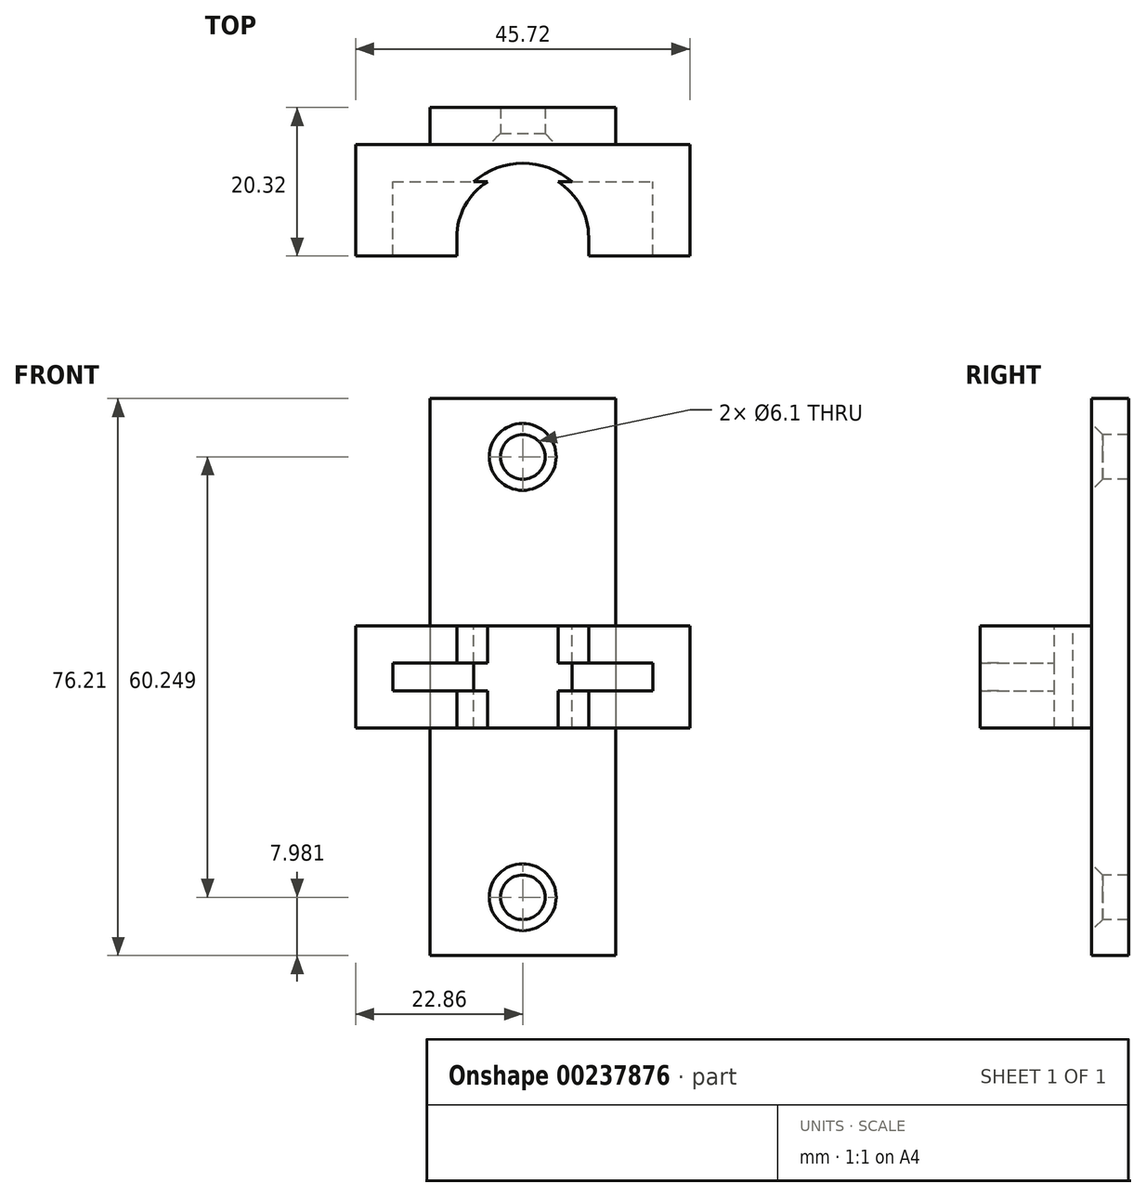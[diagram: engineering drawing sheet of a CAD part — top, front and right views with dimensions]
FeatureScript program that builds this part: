
annotation { "Feature Type Name" : "Feature", "Feature Type Description" : "" }
export const myFeature = defineFeature(function(context is Context, id is Id, definition is map)
    precondition{}
    {
        {
            var Q0;
            Q0=qCreatedBy(makeId("Top.planeOp"),FACE);
            var sketch = newSketch(context, id + "F0", { "sketchPlane" : qUnion([Q0])});
            skCircle(sketch, "E0", {"center": v(0, -0.94) * mm, "radius": 9.02 * mm});
            skCircle(sketch, "E1", {"center": v(0, -0.94) * mm, "radius": 10.16 * mm});
            skLineSegment(sketch, "E2.top", {"start": v(22.86, 11.76) * mm, "end": v(-22.86, 11.76) * mm});
            skLineSegment(sketch, "E2.left", {"start": v(22.86, -3.48) * mm, "end": v(22.86, 11.76) * mm});
            skLineSegment(sketch, "E2.right", {"start": v(-22.86, -3.48) * mm, "end": v(-22.86, 11.76) * mm});
            skPoint(sketch, "E3", {"position": v(0, -3.48) * mm});
            skLineSegment(sketch, "E4", {"start": v(-22.86, -3.48) * mm, "end": v(22.86, -3.48) * mm});
            skLineSegment(sketch, "E5", {"start": v(-10.16, -0.94) * mm, "end": v(-10.16, -3.48) * mm});
            skLineSegment(sketch, "E6", {"start": v(10.16, -0.94) * mm, "end": v(10.16, -3.48) * mm});
            skLineSegment(sketch, "E7.bottom", {"start": v(-17.78, -3.48) * mm, "end": v(17.78, -3.48) * mm});
            skLineSegment(sketch, "E7.top", {"start": v(-17.78, 6.68) * mm, "end": v(17.78, 6.68) * mm});
            skLineSegment(sketch, "E7.left", {"start": v(-17.78, -3.48) * mm, "end": v(-17.78, 6.68) * mm});
            skLineSegment(sketch, "E7.right", {"start": v(17.78, -3.48) * mm, "end": v(17.78, 6.68) * mm});
            skLineSegment(sketch, "E8", {"start": v(-9.02, -0.94) * mm, "end": v(-9.02, -3.48) * mm, "construction": true});
            skLineSegment(sketch, "E9", {"start": v(9.02, -0.94) * mm, "end": v(9.02, -3.48) * mm, "construction": true});
            skLineSegment(sketch, "E10.bottom", {"start": v(-9.02, -0.94) * mm, "end": v(9.02, -0.94) * mm});
            skLineSegment(sketch, "E10.top", {"start": v(-9.02, -3.48) * mm, "end": v(9.02, -3.48) * mm});
            skLineSegment(sketch, "E10.left", {"start": v(-9.02, -0.94) * mm, "end": v(-9.02, -3.48) * mm});
            skLineSegment(sketch, "E10.right", {"start": v(9.02, -0.94) * mm, "end": v(9.02, -3.48) * mm});
            skSolve(sketch);
        }
        {
            var Q0;
            {var subQ1=sQuery(id+"F0.wireOp",EDGE,"E5");Q0=makeQuery(id+"F0.imprint","IMPRINT",FACE,{"disambiguationData":[TD([[makeQuery(id+"F0.imprint","IMPRINT",EDGE,{"derivedFrom":subQ1}),-1.0]])]});}
            var Q1;
            {var subQ5=sQuery(id+"F0.wireOp",EDGE,"E6");Q1=makeQuery(id+"F0.imprint","IMPRINT",FACE,{"disambiguationData":[TD([[makeQuery(id+"F0.imprint","IMPRINT",EDGE,{"derivedFrom":subQ5}),1.0]])]});}
            var Q2;
            {var subQ0=sQuery(id+"F0.wireOp",EDGE,"E10.left");Q2=makeQuery(id+"F0.imprint","IMPRINT",FACE,{"disambiguationData":[TD([[makeQuery(id+"F0.imprint","IMPRINT",EDGE,{"derivedFrom":subQ0}),-1.0]])]});}
            var Q3;
            {var subQ4=sQuery(id+"F0.wireOp",EDGE,"E10.right");Q3=makeQuery(id+"F0.imprint","IMPRINT",FACE,{"disambiguationData":[TD([[makeQuery(id+"F0.imprint","IMPRINT",EDGE,{"derivedFrom":subQ4}),1.0]])]});}
            var Q4;
            {var subQ0=sQuery(id+"F0.wireOp",EDGE,"E7.top");var subQ1=sQuery(id+"F0.wireOp",EDGE,"E0");var subQ2=makeQuery(id+"F0.imprint","INTERSECT",VERTEX,{"disambiguationData":[OD(0.0)],"derivedFrom":[subQ1,subQ0]});Q4=makeQuery(id+"F0.imprint","IMPRINT",FACE,{"disambiguationData":[TD([[makeQuery(id+"F0.imprint","IMPRINT",EDGE,{"disambiguationData":[TD([[subQ2,-1.0]])],"derivedFrom":subQ1}),-1.0]])]});}
            var Q5;
            {var subQ0=sQuery(id+"F0.wireOp",EDGE,"E5");Q5=makeQuery(id+"F0.imprint","IMPRINT",FACE,{"disambiguationData":[TD([[makeQuery(id+"F0.imprint","IMPRINT",EDGE,{"derivedFrom":subQ0}),1.0]])]});}
            var Q6;
            {var subQ0=sQuery(id+"F0.wireOp",EDGE,"E6");Q6=makeQuery(id+"F0.imprint","IMPRINT",FACE,{"disambiguationData":[TD([[makeQuery(id+"F0.imprint","IMPRINT",EDGE,{"derivedFrom":subQ0}),-1.0]])]});}
            extrude(context, id + "F1", {"entities" : qUnion([Q0, Q1, Q2, Q3, Q4, Q5, Q6]), "oppositeDirection" : true, "depth" : 5.08 * mm});
        }
        {
            var Q0;
            Q0=makeQuery(id+"F0.imprint","IMPRINT",FACE,{"disambiguationData":[TD([[makeQuery(id+"F0.imprint","IMPRINT",EDGE,{"derivedFrom":sQuery(id+"F0.wireOp",EDGE,"E2.top")}),1.0]])]});
            extrude(context, id + "F2", {"entities" : qUnion([Q0]), "operationType" : NewBodyOperationType.ADD, "oppositeDirection" : true, "depth" : 13.97 * mm});
        }
        {
            var Q0;
            Q0=makeQuery(id+"F1.opExtrude","CAP_FACE",FACE,{"disambiguationData":[OSD([sQuery(id+"F0.wireOp",EDGE,"E0"),sQuery(id+"F0.wireOp",EDGE,"E1"),sQuery(id+"F0.wireOp",EDGE,"E7.bottom"),sQuery(id+"F0.wireOp",EDGE,"E7.top"),sQuery(id+"F0.wireOp",EDGE,"E7.left"),sQuery(id+"F0.wireOp",EDGE,"E7.right"),sQuery(id+"F0.wireOp",EDGE,"E10.left"),sQuery(id+"F0.wireOp",EDGE,"E10.right")])],"isStart":false});
            extrude(context, id + "F3", {"entities" : qUnion([Q0]), "operationType" : NewBodyOperationType.ADD, "depth" : 8.9 * mm, "hasSecondDirection" : true, "secondDirectionOppositeDirection" : false, "secondDirectionDepth" : 3.8 * mm});
        }
        {
            var Q0;
            Q0=makeQuery(id+"F2.opExtrude","SWEPT_FACE",FACE,{"disambiguationData":[OSD([sQuery(id+"F0.wireOp",EDGE,"E2.top")])]});
            var sketch = newSketch(context, id + "F4", { "sketchPlane" : qUnion([Q0])});
            skLineSegment(sketch, "E11.bottom", {"start": v(12.7, 31.12) * mm, "end": v(12.7, -45.09) * mm});
            skLineSegment(sketch, "E11.top", {"start": v(-12.7, 31.11) * mm, "end": v(-12.7, -45.09) * mm});
            skLineSegment(sketch, "E11.left", {"start": v(12.7, 31.12) * mm, "end": v(-12.7, 31.12) * mm});
            skLineSegment(sketch, "E11.right", {"start": v(12.7, -45.09) * mm, "end": v(-12.7, -45.09) * mm});
            skPoint(sketch, "E11.middle", {"position": v(0, -6.99) * mm});
            skPoint(sketch, "E11.middle.positionSnap0", {"position": v(0, 15.16) * mm});
            skPoint(sketch, "E11.middle.positionSnap1", {"position": v(6.99, -6.99) * mm});
            skPoint(sketch, "E11.centerSnap0", {"position": v(0, 15.15) * mm});
            skPoint(sketch, "E11.centerSnap1", {"position": v(-62.18, -6.99) * mm});
            skLineSegment(sketch, "E12", {"start": v(0, 15.16) * mm, "end": v(0, 31.11) * mm, "construction": true});
            skCircle(sketch, "E13", {"center": v(0, 23.14) * mm, "radius": 3.05 * mm});
            skLineSegment(sketch, "E14", {"start": v(6.99, -6.99) * mm, "end": v(0, -6.99) * mm, "construction": true});
            skCircle(sketch, "E15.MirrorC", {"center": v(0, -37.1) * mm, "radius": 3.05 * mm});
            skLineSegment(sketch, "E16.bottom", {"start": v(0, 0) * mm, "end": v(22.86, 0) * mm});
            skLineSegment(sketch, "E16.top", {"start": v(0, -13.97) * mm, "end": v(22.86, -13.97) * mm});
            skLineSegment(sketch, "E16.left", {"start": v(0, 0) * mm, "end": v(0, -13.97) * mm});
            skLineSegment(sketch, "E16.right", {"start": v(22.86, 0) * mm, "end": v(22.86, -13.97) * mm});
            skLineSegment(sketch, "E17.bottom", {"start": v(22.86, -13.97) * mm, "end": v(0, -13.97) * mm});
            skLineSegment(sketch, "E17.top", {"start": v(22.86, -6.99) * mm, "end": v(0, -6.99) * mm});
            skLineSegment(sketch, "E17.left", {"start": v(22.86, -13.97) * mm, "end": v(22.86, -6.99) * mm});
            skLineSegment(sketch, "E17.right", {"start": v(0, -13.97) * mm, "end": v(0, -6.99) * mm});
            skLineSegment(sketch, "E18.bottom", {"start": v(12.7, -13.97) * mm, "end": v(-12.7, -13.97) * mm});
            skLineSegment(sketch, "E18.top", {"start": v(12.7, 0) * mm, "end": v(-12.7, 0) * mm});
            skLineSegment(sketch, "E18.left", {"start": v(12.7, -13.97) * mm, "end": v(12.7, 0) * mm});
            skLineSegment(sketch, "E18.right", {"start": v(-12.7, -13.97) * mm, "end": v(-12.7, 0) * mm});
            skSolve(sketch);
        }
        {
            var Q0;
            {var subQ0=sQuery(id+"F4.wireOp",EDGE,"E11.left");Q0=makeQuery(id+"F4.imprint","IMPRINT",FACE,{"disambiguationData":[TD([[makeQuery(id+"F4.imprint","IMPRINT",EDGE,{"derivedFrom":subQ0}),1.0]])]});}
            var Q1;
            {var subQ0=sQuery(id+"F4.wireOp",EDGE,"E11.right");Q1=makeQuery(id+"F4.imprint","IMPRINT",FACE,{"disambiguationData":[TD([[makeQuery(id+"F4.imprint","IMPRINT",EDGE,{"derivedFrom":subQ0}),-1.0]])]});}
            var Q2;
            {var subQ0=sQuery(id+"F4.wireOp",EDGE,"E17.right");Q2=makeQuery(id+"F4.imprint","IMPRINT",FACE,{"disambiguationData":[TD([[makeQuery(id+"F4.imprint","IMPRINT",EDGE,{"derivedFrom":subQ0}),-1.0]])]});}
            var Q3;
            {var subQ1=sQuery(id+"F4.wireOp",EDGE,"E16.left");Q3=makeQuery(id+"F4.imprint","IMPRINT",FACE,{"disambiguationData":[TD([[makeQuery(id+"F4.imprint","IMPRINT",EDGE,{"derivedFrom":subQ1}),-1.0]])]});}
            var Q4;
            {var subQ0=sQuery(id+"F4.wireOp",EDGE,"E16.left");Q4=makeQuery(id+"F4.imprint","IMPRINT",FACE,{"disambiguationData":[TD([[makeQuery(id+"F4.imprint","IMPRINT",EDGE,{"derivedFrom":subQ0}),1.0]])]});}
            extrude(context, id + "F5", {"entities" : qUnion([Q0, Q1, Q2, Q3, Q4]), "operationType" : NewBodyOperationType.ADD, "depth" : 5.08 * mm});
        }
        {
            var Q0;
            Q0=makeQuery(id+"F5.opExtrude","CAP_EDGE",EDGE,{"disambiguationData":[OSD([sQuery(id+"F4.wireOp",EDGE,"E13")])],"isStart":true});
            var Q1;
            Q1=makeQuery(id+"F5.opExtrude","CAP_EDGE",EDGE,{"disambiguationData":[OSD([sQuery(id+"F4.wireOp",EDGE,"E15.MirrorC")])],"isStart":true});
            chamfer(context, id + "F6", {"entities" : qUnion([Q0, Q1]), "width" : 1.52 * mm, "tangentPropagation" : true});
        }
    });
